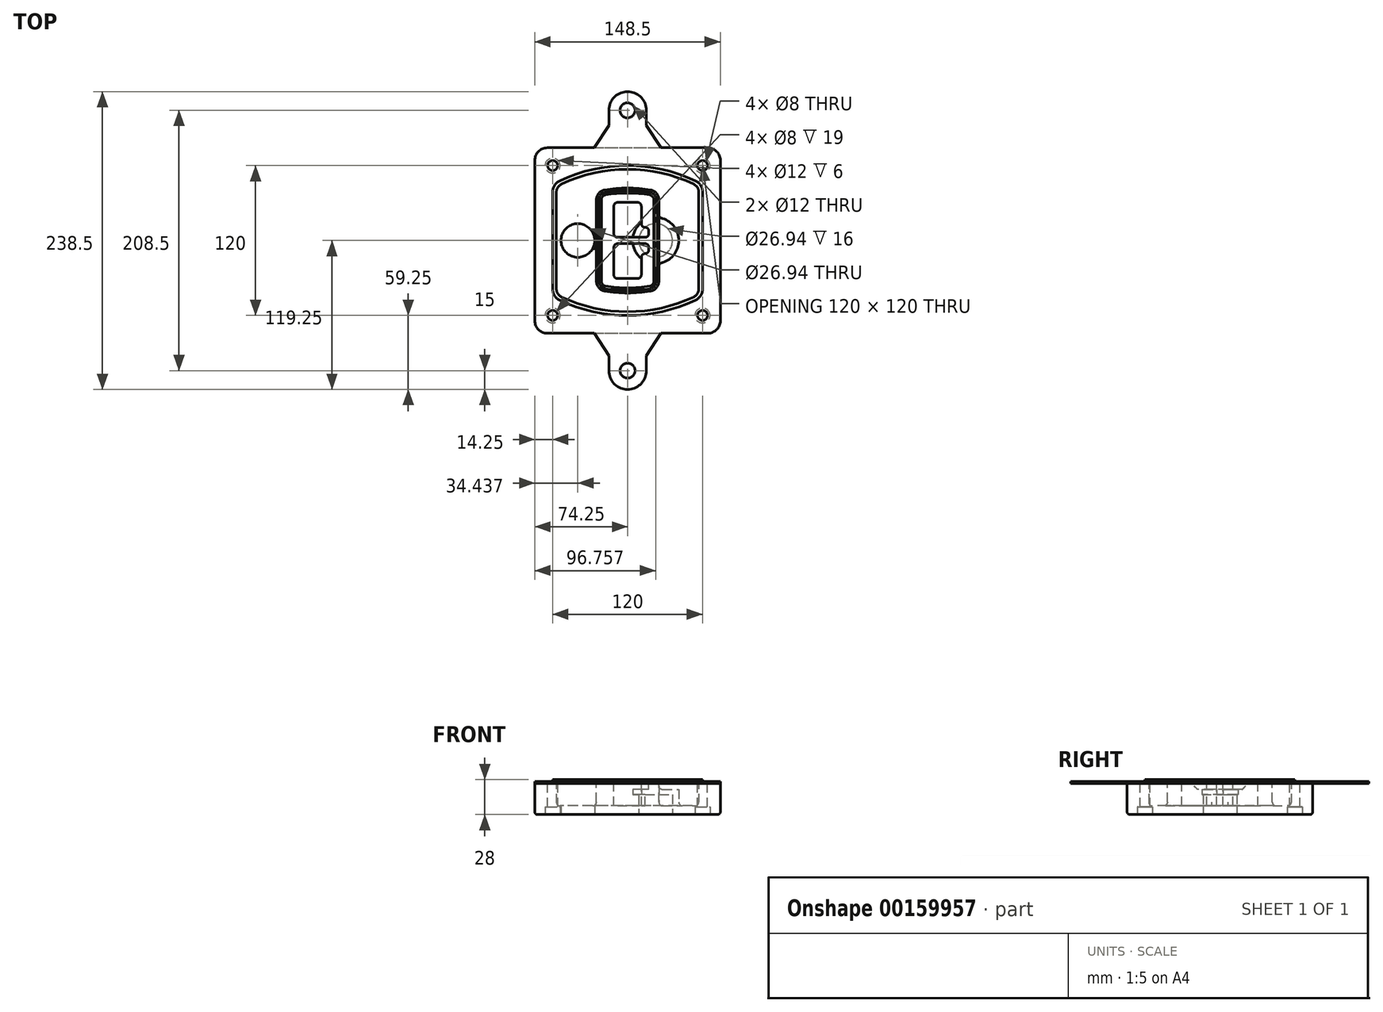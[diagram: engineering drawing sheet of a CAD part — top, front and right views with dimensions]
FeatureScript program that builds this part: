
annotation { "Feature Type Name" : "Feature", "Feature Type Description" : "" }
export const myFeature = defineFeature(function(context is Context, id is Id, definition is map)
    precondition{}
    {
        {
            var Q0;
            Q0=qCreatedBy(makeId("Top.planeOp"),FACE);
            var sketch = newSketch(context, id + "F0", { "sketchPlane" : qUnion([Q0])});
            skPoint(sketch, "E0.rect.middle", {"position": v(0, 0) * mm});
            skLineSegment(sketch, "E1.bottom", {"start": v(-64.25, -74.25) * mm, "end": v(64.25, -74.25) * mm});
            skLineSegment(sketch, "E1.top", {"start": v(-64.25, 74.25) * mm, "end": v(64.25, 74.25) * mm});
            skLineSegment(sketch, "E1.left", {"start": v(-74.25, -64.25) * mm, "end": v(-74.25, 64.25) * mm});
            skLineSegment(sketch, "E1.right", {"start": v(74.25, -64.25) * mm, "end": v(74.25, 64.25) * mm});
            skLineSegment(sketch, "E2", {"start": v(-74.25, 74.25) * mm, "end": v(74.25, -74.25) * mm, "construction": true});
            skLineSegment(sketch, "E3", {"start": v(74.25, 74.25) * mm, "end": v(-74.25, -74.25) * mm, "construction": true});
            skCircle(sketch, "E4", {"center": v(-60, 60) * mm, "radius": 4 * mm});
            skCircle(sketch, "E5", {"center": v(60, 60) * mm, "radius": 4 * mm});
            skCircle(sketch, "E6", {"center": v(60, -60) * mm, "radius": 4 * mm});
            skCircle(sketch, "E7", {"center": v(-60, -60) * mm, "radius": 4 * mm});
            skLineSegment(sketch, "E8", {"start": v(-60, 60) * mm, "end": v(60, 60) * mm, "construction": true});
            skLineSegment(sketch, "E9", {"start": v(60, 60) * mm, "end": v(60, -60) * mm, "construction": true});
            skLineSegment(sketch, "E10", {"start": v(60, -60) * mm, "end": v(-60, -60) * mm, "construction": true});
            skLineSegment(sketch, "E11", {"start": v(-60, -60) * mm, "end": v(-60, 60) * mm, "construction": true});
            skLineSegment(sketch, "E12", {"start": v(-60, 38.83) * mm, "end": v(-60, -38.83) * mm});
            skLineSegment(sketch, "E13", {"start": v(60, 38.83) * mm, "end": v(60, -38.83) * mm});
            skArc(sketch, "E14", {"start": v(54.26, 47.88) * mm, "mid": v(0, 60) * mm, "end": v(-54.26, 47.88) * mm});
            skArc(sketch, "E15", {"start": v(-54.26, -47.88) * mm, "mid": v(0, -60) * mm, "end": v(54.26, -47.88) * mm});
            skLineSegment(sketch, "E16", {"start": v(-60, 0) * mm, "end": v(60, 0) * mm, "construction": true});
            skPoint(sketch, "E17.visualSharp", {"position": v(-60, -45) * mm});
            skArc(sketch, "E17.filletArc", {"start": v(-60, -38.83) * mm, "mid": v(-58.44, -44.2) * mm, "end": v(-54.26, -47.88) * mm});
            skPoint(sketch, "E18.visualSharp", {"position": v(-60, 45) * mm});
            skArc(sketch, "E18.filletArc", {"start": v(-54.26, 47.88) * mm, "mid": v(-58.44, 44.2) * mm, "end": v(-60, 38.83) * mm});
            skPoint(sketch, "E19.visualSharp", {"position": v(60, 45) * mm});
            skArc(sketch, "E19.filletArc", {"start": v(60, 38.83) * mm, "mid": v(58.44, 44.2) * mm, "end": v(54.26, 47.88) * mm});
            skPoint(sketch, "E20.visualSharp", {"position": v(60, -45) * mm});
            skArc(sketch, "E20.filletArc", {"start": v(54.26, -47.88) * mm, "mid": v(58.44, -44.2) * mm, "end": v(60, -38.83) * mm});
            skPoint(sketch, "E21.visualSharp", {"position": v(-74.25, 74.25) * mm});
            skArc(sketch, "E21.filletArc", {"start": v(-64.25, 74.25) * mm, "mid": v(-71.32, 71.32) * mm, "end": v(-74.25, 64.25) * mm});
            skPoint(sketch, "E22.visualSharp", {"position": v(74.25, 74.25) * mm});
            skArc(sketch, "E22.filletArc", {"start": v(74.25, 64.25) * mm, "mid": v(71.32, 71.32) * mm, "end": v(64.25, 74.25) * mm});
            skPoint(sketch, "E23.visualSharp", {"position": v(74.25, -74.25) * mm});
            skArc(sketch, "E23.filletArc", {"start": v(64.25, -74.25) * mm, "mid": v(71.32, -71.32) * mm, "end": v(74.25, -64.25) * mm});
            skPoint(sketch, "E24.visualSharp", {"position": v(-74.25, -74.25) * mm});
            skArc(sketch, "E24.filletArc", {"start": v(-74.25, -64.25) * mm, "mid": v(-71.32, -71.32) * mm, "end": v(-64.25, -74.25) * mm});
            skArc(sketch, "E25.0", {"start": v(57, 38.83) * mm, "mid": v(55.9, 42.58) * mm, "end": v(52.98, 45.17) * mm});
            skLineSegment(sketch, "E25.1", {"start": v(57, 38.83) * mm, "end": v(57, -38.83) * mm});
            skArc(sketch, "E25.2", {"start": v(52.98, -45.17) * mm, "mid": v(55.9, -42.58) * mm, "end": v(57, -38.83) * mm});
            skArc(sketch, "E25.3", {"start": v(-52.98, -45.17) * mm, "mid": v(0, -57) * mm, "end": v(52.98, -45.17) * mm});
            skArc(sketch, "E25.4", {"start": v(-57, -38.83) * mm, "mid": v(-55.9, -42.58) * mm, "end": v(-52.98, -45.17) * mm});
            skArc(sketch, "E25.5", {"start": v(52.98, 45.17) * mm, "mid": v(0, 57) * mm, "end": v(-52.98, 45.17) * mm});
            skLineSegment(sketch, "E25.6", {"start": v(-57, 38.83) * mm, "end": v(-57, -38.83) * mm});
            skArc(sketch, "E25.7", {"start": v(-52.98, 45.17) * mm, "mid": v(-55.9, 42.58) * mm, "end": v(-57, 38.83) * mm});
            skArc(sketch, "E26.0", {"start": v(-55.96, 51.5) * mm, "mid": v(-61.82, 46.33) * mm, "end": v(-64, 38.83) * mm});
            skArc(sketch, "E26.1", {"start": v(55.96, 51.5) * mm, "mid": v(0, 64) * mm, "end": v(-55.96, 51.5) * mm});
            skArc(sketch, "E26.2", {"start": v(64, 38.83) * mm, "mid": v(61.82, 46.33) * mm, "end": v(55.96, 51.5) * mm});
            skLineSegment(sketch, "E26.3", {"start": v(64, 38.83) * mm, "end": v(64, -38.83) * mm});
            skArc(sketch, "E26.4", {"start": v(55.96, -51.5) * mm, "mid": v(61.82, -46.33) * mm, "end": v(64, -38.83) * mm});
            skLineSegment(sketch, "E26.5", {"start": v(-64, 38.83) * mm, "end": v(-64, -38.83) * mm});
            skArc(sketch, "E26.6", {"start": v(-55.96, -51.5) * mm, "mid": v(0, -64) * mm, "end": v(55.96, -51.5) * mm});
            skArc(sketch, "E26.7", {"start": v(-64, -38.83) * mm, "mid": v(-61.82, -46.33) * mm, "end": v(-55.96, -51.5) * mm});
            skSolve(sketch);
        }
        {
            var Q0;
            Q0=makeQuery(id+"F0.imprint","IMPRINT",FACE,{"disambiguationData":[TD([[makeQuery(id+"F0.imprint","IMPRINT",EDGE,{"derivedFrom":sQuery(id+"F0.wireOp",EDGE,"E1.bottom")}),1.0]])]});
            var Q1;
            Q1=makeQuery(id+"F0.imprint","IMPRINT",FACE,{"disambiguationData":[TD([[makeQuery(id+"F0.imprint","IMPRINT",EDGE,{"derivedFrom":sQuery(id+"F0.wireOp",EDGE,"E12")}),1.0]])]});
            var Q2;
            Q2=makeQuery(id+"F0.imprint","IMPRINT",FACE,{"disambiguationData":[TD([[makeQuery(id+"F0.imprint","IMPRINT",EDGE,{"derivedFrom":sQuery(id+"F0.wireOp",EDGE,"E25.0")}),1.0]])]});
            var Q3;
            Q3=makeQuery(id+"F0.imprint","IMPRINT",FACE,{"disambiguationData":[TD([[makeQuery(id+"F0.imprint","IMPRINT",EDGE,{"derivedFrom":sQuery(id+"F0.wireOp",EDGE,"E12")}),-1.0]])]});
            extrude(context, id + "F1", {"entities" : qUnion([Q0, Q1, Q2, Q3]), "oppositeDirection" : true, "depth" : 25 * mm});
        }
        {
            var Q0;
            Q0=makeQuery(id+"F0.imprint","IMPRINT",FACE,{"disambiguationData":[TD([[makeQuery(id+"F0.imprint","IMPRINT",EDGE,{"derivedFrom":sQuery(id+"F0.wireOp",EDGE,"E12")}),1.0]])]});
            extrude(context, id + "F2", {"entities" : qUnion([Q0]), "operationType" : NewBodyOperationType.ADD, "depth" : 3 * mm});
        }
        {
            var Q0;
            Q0=makeQuery(id+"F0.imprint","IMPRINT",FACE,{"disambiguationData":[TD([[makeQuery(id+"F0.imprint","IMPRINT",EDGE,{"derivedFrom":sQuery(id+"F0.wireOp",EDGE,"E25.0")}),1.0]])]});
            extrude(context, id + "F3", {"entities" : qUnion([Q0]), "operationType" : NewBodyOperationType.REMOVE, "oppositeDirection" : true, "depth" : 18 * mm});
        }
        {
            var Q0;
            Q0=makeQuery(id+"F2.opExtrude","CAP_FACE",FACE,{"disambiguationData":[OSD([sQuery(id+"F0.wireOp",EDGE,"E12"),sQuery(id+"F0.wireOp",EDGE,"E13"),sQuery(id+"F0.wireOp",EDGE,"E14"),sQuery(id+"F0.wireOp",EDGE,"E15"),sQuery(id+"F0.wireOp",EDGE,"E17.filletArc"),sQuery(id+"F0.wireOp",EDGE,"E18.filletArc"),sQuery(id+"F0.wireOp",EDGE,"E19.filletArc"),sQuery(id+"F0.wireOp",EDGE,"E20.filletArc"),sQuery(id+"F0.wireOp",EDGE,"E25.0"),sQuery(id+"F0.wireOp",EDGE,"E25.1"),sQuery(id+"F0.wireOp",EDGE,"E25.2"),sQuery(id+"F0.wireOp",EDGE,"E25.3"),sQuery(id+"F0.wireOp",EDGE,"E25.4"),sQuery(id+"F0.wireOp",EDGE,"E25.5"),sQuery(id+"F0.wireOp",EDGE,"E25.6"),sQuery(id+"F0.wireOp",EDGE,"E25.7")])],"isStart":false});
            var sketch = newSketch(context, id + "F4", { "sketchPlane" : qUnion([Q0])});
            skArc(sketch, "E27.0", {"start": v(-18.34, -40.45) * mm, "mid": v(0, -42) * mm, "end": v(18.34, -40.45) * mm});
            skArc(sketch, "E28.0", {"start": v(18.34, 40.45) * mm, "mid": v(0, 42) * mm, "end": v(-18.34, 40.45) * mm});
            skLineSegment(sketch, "E29", {"start": v(-25, 32.57) * mm, "end": v(-25, -32.57) * mm});
            skLineSegment(sketch, "E30", {"start": v(25, 32.57) * mm, "end": v(25, -32.57) * mm});
            skLineSegment(sketch, "E31", {"start": v(-25, 39.1) * mm, "end": v(25, 39.1) * mm, "construction": true});
            skLineSegment(sketch, "E32", {"start": v(-25, -39.1) * mm, "end": v(25, -39.1) * mm, "construction": true});
            skPoint(sketch, "E33.visualSharp", {"position": v(-25, 39.1) * mm});
            skArc(sketch, "E33.filletArc", {"start": v(-18.34, 40.45) * mm, "mid": v(-23.11, 37.73) * mm, "end": v(-25, 32.57) * mm});
            skPoint(sketch, "E34.visualSharp", {"position": v(25, 39.1) * mm});
            skArc(sketch, "E34.filletArc", {"start": v(25, 32.57) * mm, "mid": v(23.11, 37.73) * mm, "end": v(18.34, 40.45) * mm});
            skPoint(sketch, "E35.visualSharp", {"position": v(25, -39.1) * mm});
            skArc(sketch, "E35.filletArc", {"start": v(18.34, -40.45) * mm, "mid": v(23.11, -37.73) * mm, "end": v(25, -32.57) * mm});
            skPoint(sketch, "E36.visualSharp", {"position": v(-25, -39.1) * mm});
            skArc(sketch, "E36.filletArc", {"start": v(-25, -32.57) * mm, "mid": v(-23.11, -37.73) * mm, "end": v(-18.34, -40.45) * mm});
            skArc(sketch, "E37.0", {"start": v(52.98, 45.17) * mm, "mid": v(0, 57) * mm, "end": v(-52.98, 45.17) * mm});
            skArc(sketch, "E37.1", {"start": v(-52.98, 45.17) * mm, "mid": v(-55.9, 42.58) * mm, "end": v(-57, 38.83) * mm});
            skLineSegment(sketch, "E37.2", {"start": v(-57, 38.83) * mm, "end": v(-57, -38.83) * mm});
            skArc(sketch, "E37.3", {"start": v(-57, -38.83) * mm, "mid": v(-55.9, -42.58) * mm, "end": v(-52.98, -45.17) * mm});
            skArc(sketch, "E37.4", {"start": v(-52.98, -45.17) * mm, "mid": v(0, -57) * mm, "end": v(52.98, -45.17) * mm});
            skArc(sketch, "E37.5", {"start": v(52.98, -45.17) * mm, "mid": v(55.9, -42.58) * mm, "end": v(57, -38.83) * mm});
            skLineSegment(sketch, "E37.6", {"start": v(57, 38.83) * mm, "end": v(57, -38.83) * mm});
            skArc(sketch, "E37.7", {"start": v(57, 38.83) * mm, "mid": v(55.9, 42.58) * mm, "end": v(52.98, 45.17) * mm});
            skLineSegment(sketch, "E38.0", {"start": v(23, 32.57) * mm, "end": v(23, -32.57) * mm});
            skArc(sketch, "E38.1", {"start": v(18, -38.48) * mm, "mid": v(21.58, -36.44) * mm, "end": v(23, -32.57) * mm});
            skArc(sketch, "E38.2", {"start": v(-18, -38.48) * mm, "mid": v(0, -40) * mm, "end": v(18, -38.48) * mm});
            skArc(sketch, "E38.3", {"start": v(-23, -32.57) * mm, "mid": v(-21.58, -36.44) * mm, "end": v(-18, -38.48) * mm});
            skLineSegment(sketch, "E38.4", {"start": v(-23, 32.57) * mm, "end": v(-23, -32.57) * mm});
            skArc(sketch, "E38.5", {"start": v(23, 32.57) * mm, "mid": v(21.58, 36.44) * mm, "end": v(18, 38.48) * mm});
            skArc(sketch, "E38.6", {"start": v(-18, 38.48) * mm, "mid": v(-21.58, 36.44) * mm, "end": v(-23, 32.57) * mm});
            skArc(sketch, "E38.7", {"start": v(18, 38.48) * mm, "mid": v(0, 40) * mm, "end": v(-18, 38.48) * mm});
            skArc(sketch, "E39.0", {"start": v(21, 32.57) * mm, "mid": v(20.06, 35.15) * mm, "end": v(17.67, 36.5) * mm});
            skLineSegment(sketch, "E39.1", {"start": v(21, 32.57) * mm, "end": v(21, -32.57) * mm});
            skArc(sketch, "E39.2", {"start": v(17.67, -36.5) * mm, "mid": v(20.06, -35.15) * mm, "end": v(21, -32.57) * mm});
            skArc(sketch, "E39.3", {"start": v(-17.67, -36.5) * mm, "mid": v(0, -38) * mm, "end": v(17.67, -36.5) * mm});
            skArc(sketch, "E39.4", {"start": v(-21, -32.57) * mm, "mid": v(-20.06, -35.15) * mm, "end": v(-17.67, -36.5) * mm});
            skArc(sketch, "E39.5", {"start": v(17.67, 36.5) * mm, "mid": v(0, 38) * mm, "end": v(-17.67, 36.5) * mm});
            skLineSegment(sketch, "E39.6", {"start": v(-21, 32.57) * mm, "end": v(-21, -32.57) * mm});
            skArc(sketch, "E39.7", {"start": v(-17.67, 36.5) * mm, "mid": v(-20.06, 35.15) * mm, "end": v(-21, 32.57) * mm});
            skLineSegment(sketch, "E40", {"start": v(-25, 0) * mm, "end": v(25, 0) * mm, "construction": true});
            skLineSegment(sketch, "E41", {"start": v(-11, 5.5) * mm, "end": v(-11, 27.5) * mm});
            skLineSegment(sketch, "E42", {"start": v(-8, 30.5) * mm, "end": v(8, 30.5) * mm});
            skLineSegment(sketch, "E43", {"start": v(11, 27.5) * mm, "end": v(11, 13.5) * mm});
            skLineSegment(sketch, "E44", {"start": v(14, 10.5) * mm, "end": v(14, 10.5) * mm});
            skLineSegment(sketch, "E45", {"start": v(17, 7.5) * mm, "end": v(17, 5.5) * mm});
            skLineSegment(sketch, "E46", {"start": v(14, 2.5) * mm, "end": v(-8, 2.5) * mm});
            skPoint(sketch, "E47.visualSharp", {"position": v(-11, 30.5) * mm});
            skArc(sketch, "E47.filletArc", {"start": v(-8, 30.5) * mm, "mid": v(-10.12, 29.62) * mm, "end": v(-11, 27.5) * mm});
            skPoint(sketch, "E48.visualSharp", {"position": v(11, 30.5) * mm});
            skArc(sketch, "E48.filletArc", {"start": v(11, 27.5) * mm, "mid": v(10.12, 29.62) * mm, "end": v(8, 30.5) * mm});
            skPoint(sketch, "E49.visualSharp", {"position": v(11, 10.5) * mm});
            skArc(sketch, "E49.filletArc", {"start": v(11, 13.5) * mm, "mid": v(11.88, 11.38) * mm, "end": v(14, 10.5) * mm});
            skPoint(sketch, "E50.visualSharp", {"position": v(17, 10.5) * mm});
            skArc(sketch, "E50.filletArc", {"start": v(17, 7.5) * mm, "mid": v(16.12, 9.62) * mm, "end": v(14, 10.5) * mm});
            skPoint(sketch, "E51.visualSharp", {"position": v(17, 2.5) * mm});
            skArc(sketch, "E51.filletArc", {"start": v(14, 2.5) * mm, "mid": v(16.12, 3.38) * mm, "end": v(17, 5.5) * mm});
            skPoint(sketch, "E52.visualSharp", {"position": v(-11, 2.5) * mm});
            skArc(sketch, "E52.filletArc", {"start": v(-11, 5.5) * mm, "mid": v(-10.12, 3.38) * mm, "end": v(-8, 2.5) * mm});
            skLineSegment(sketch, "E53.0.MirrorCS", {"start": v(14, -2.5) * mm, "end": v(-8, -2.5) * mm});
            skArc(sketch, "E54.0.MirrorCS", {"start": v(-11, -5.5) * mm, "mid": v(-10.12, -3.38) * mm, "end": v(-8, -2.5) * mm});
            skLineSegment(sketch, "E55.0.MirrorCS", {"start": v(-11, -5.5) * mm, "end": v(-11, -27.5) * mm});
            skArc(sketch, "E56.0.MirrorCS", {"start": v(-8, -30.5) * mm, "mid": v(-10.12, -29.62) * mm, "end": v(-11, -27.5) * mm});
            skLineSegment(sketch, "E57.0.MirrorCS", {"start": v(-8, -30.5) * mm, "end": v(8, -30.5) * mm});
            skArc(sketch, "E58.0.MirrorCS", {"start": v(11, -27.5) * mm, "mid": v(10.12, -29.62) * mm, "end": v(8, -30.5) * mm});
            skLineSegment(sketch, "E59.0.MirrorCS", {"start": v(11, -27.5) * mm, "end": v(11, -13.5) * mm});
            skArc(sketch, "E60.0.MirrorCS", {"start": v(11, -13.5) * mm, "mid": v(11.88, -11.38) * mm, "end": v(14, -10.5) * mm});
            skArc(sketch, "E61.0.MirrorCS", {"start": v(17, -7.5) * mm, "mid": v(16.12, -9.62) * mm, "end": v(14, -10.5) * mm});
            skLineSegment(sketch, "E62.0.MirrorCS", {"start": v(17, -7.5) * mm, "end": v(17, -5.5) * mm});
            skArc(sketch, "E63.0.MirrorCS", {"start": v(14, -2.5) * mm, "mid": v(16.12, -3.38) * mm, "end": v(17, -5.5) * mm});
            skSolve(sketch);
        }
        {
            var Q0;
            Q0=makeQuery(id+"F4.imprint","IMPRINT",FACE,{"disambiguationData":[TD([[makeQuery(id+"F4.imprint","IMPRINT",EDGE,{"derivedFrom":sQuery(id+"F4.wireOp",EDGE,"E27.0")}),1.0]])]});
            var Q1;
            Q1=makeQuery(id+"F4.imprint","IMPRINT",FACE,{"disambiguationData":[TD([[makeQuery(id+"F4.imprint","IMPRINT",EDGE,{"derivedFrom":sQuery(id+"F4.wireOp",EDGE,"E38.0")}),-1.0]])]});
            var Q2;
            Q2=makeQuery(id+"F4.imprint","IMPRINT",FACE,{"disambiguationData":[TD([[makeQuery(id+"F4.imprint","IMPRINT",EDGE,{"derivedFrom":sQuery(id+"F4.wireOp",EDGE,"E39.0")}),1.0]])]});
            extrude(context, id + "F5", {"entities" : qUnion([Q0, Q1, Q2]), "operationType" : NewBodyOperationType.ADD, "endBound" : BoundingType.UP_TO_NEXT, "oppositeDirection" : true, "depth" : 25 * mm});
        }
        {
            var Q0;
            Q0=makeQuery(id+"F4.imprint","IMPRINT",FACE,{"disambiguationData":[TD([[makeQuery(id+"F4.imprint","IMPRINT",EDGE,{"derivedFrom":sQuery(id+"F4.wireOp",EDGE,"E38.0")}),-1.0]])]});
            extrude(context, id + "F6", {"entities" : qUnion([Q0]), "operationType" : NewBodyOperationType.REMOVE, "oppositeDirection" : true, "depth" : 2 * mm});
        }
        {
            var Q0;
            Q0=makeQuery(id+"F1.opExtrude","CAP_FACE",FACE,{"disambiguationData":[OSD([sQuery(id+"F0.wireOp",EDGE,"E1.bottom"),sQuery(id+"F0.wireOp",EDGE,"E1.top"),sQuery(id+"F0.wireOp",EDGE,"E1.left"),sQuery(id+"F0.wireOp",EDGE,"E1.right"),sQuery(id+"F0.wireOp",EDGE,"E4"),sQuery(id+"F0.wireOp",EDGE,"E5"),sQuery(id+"F0.wireOp",EDGE,"E6"),sQuery(id+"F0.wireOp",EDGE,"E7"),sQuery(id+"F0.wireOp",EDGE,"E21.filletArc"),sQuery(id+"F0.wireOp",EDGE,"E22.filletArc"),sQuery(id+"F0.wireOp",EDGE,"E23.filletArc"),sQuery(id+"F0.wireOp",EDGE,"E24.filletArc")])],"isStart":false});
            var sketch = newSketch(context, id + "F7", { "sketchPlane" : qUnion([Q0])});
            skCircle(sketch, "E64", {"center": v(22.5, 0) * mm, "radius": 13.47 * mm});
            skCircle(sketch, "E65", {"center": v(-39.81, 0) * mm, "radius": 13.47 * mm});
            skLineSegment(sketch, "E66", {"start": v(74.25, 0) * mm, "end": v(-74.25, 0) * mm});
            skCircle(sketch, "E67", {"center": v(22.5, 0) * mm, "radius": 18.47 * mm});
            skCircle(sketch, "E68", {"center": v(60, -60) * mm, "radius": 6 * mm});
            skCircle(sketch, "E69", {"center": v(-60, -60) * mm, "radius": 6 * mm});
            skCircle(sketch, "E70", {"center": v(-60, 60) * mm, "radius": 6 * mm});
            skCircle(sketch, "E71", {"center": v(60, 60) * mm, "radius": 6 * mm});
            skSolve(sketch);
        }
        {
            var Q0;
            {var subQ1=sQuery(id+"F7.wireOp",EDGE,"E66");var subQ4=sQuery(id+"F7.wireOp",EDGE,"E64");var subQ6=makeQuery(id+"F7.imprint","INTERSECT",VERTEX,{"disambiguationData":[OD(0.0)],"derivedFrom":[subQ4,subQ1]});Q0=makeQuery(id+"F7.imprint","IMPRINT",FACE,{"disambiguationData":[TD([[makeQuery(id+"F7.imprint","IMPRINT",EDGE,{"disambiguationData":[TD([[subQ6,-1.0]])],"derivedFrom":subQ4}),-1.0]])]});}
            var Q1;
            {var subQ0=sQuery(id+"F7.wireOp",EDGE,"E66");var subQ1=sQuery(id+"F7.wireOp",EDGE,"E64");var subQ3=makeQuery(id+"F7.imprint","INTERSECT",VERTEX,{"disambiguationData":[OD(0.0)],"derivedFrom":[subQ1,subQ0]});Q1=makeQuery(id+"F7.imprint","IMPRINT",FACE,{"disambiguationData":[TD([[makeQuery(id+"F7.imprint","IMPRINT",EDGE,{"disambiguationData":[TD([[subQ3,-1.0]])],"derivedFrom":subQ1}),1.0]])]});}
            var Q2;
            {var subQ0=sQuery(id+"F7.wireOp",EDGE,"E66");var subQ1=sQuery(id+"F7.wireOp",EDGE,"E64");var subQ3=makeQuery(id+"F7.imprint","INTERSECT",VERTEX,{"disambiguationData":[OD(0.0)],"derivedFrom":[subQ1,subQ0]});Q2=makeQuery(id+"F7.imprint","IMPRINT",FACE,{"disambiguationData":[TD([[makeQuery(id+"F7.imprint","IMPRINT",EDGE,{"disambiguationData":[TD([[subQ3,1.0]])],"derivedFrom":subQ1}),1.0]])]});}
            var Q3;
            {var subQ1=sQuery(id+"F7.wireOp",EDGE,"E66");var subQ4=sQuery(id+"F7.wireOp",EDGE,"E64");var subQ6=makeQuery(id+"F7.imprint","INTERSECT",VERTEX,{"disambiguationData":[OD(0.0)],"derivedFrom":[subQ4,subQ1]});Q3=makeQuery(id+"F7.imprint","IMPRINT",FACE,{"disambiguationData":[TD([[makeQuery(id+"F7.imprint","IMPRINT",EDGE,{"disambiguationData":[TD([[subQ6,1.0]])],"derivedFrom":subQ4}),-1.0]])]});}
            extrude(context, id + "F8", {"entities" : qUnion([Q0, Q1, Q2, Q3]), "operationType" : NewBodyOperationType.ADD, "oppositeDirection" : true, "depth" : 20 * mm});
        }
        {
            var Q0;
            {var subQ0=sQuery(id+"F7.wireOp",EDGE,"E66");var subQ1=sQuery(id+"F7.wireOp",EDGE,"E64");var subQ3=makeQuery(id+"F7.imprint","INTERSECT",VERTEX,{"disambiguationData":[OD(0.0)],"derivedFrom":[subQ1,subQ0]});Q0=makeQuery(id+"F7.imprint","IMPRINT",FACE,{"disambiguationData":[TD([[makeQuery(id+"F7.imprint","IMPRINT",EDGE,{"disambiguationData":[TD([[subQ3,-1.0]])],"derivedFrom":subQ1}),1.0]])]});}
            var Q1;
            {var subQ0=sQuery(id+"F7.wireOp",EDGE,"E66");var subQ1=sQuery(id+"F7.wireOp",EDGE,"E64");var subQ3=makeQuery(id+"F7.imprint","INTERSECT",VERTEX,{"disambiguationData":[OD(0.0)],"derivedFrom":[subQ1,subQ0]});Q1=makeQuery(id+"F7.imprint","IMPRINT",FACE,{"disambiguationData":[TD([[makeQuery(id+"F7.imprint","IMPRINT",EDGE,{"disambiguationData":[TD([[subQ3,1.0]])],"derivedFrom":subQ1}),1.0]])]});}
            extrude(context, id + "F9", {"entities" : qUnion([Q0, Q1]), "operationType" : NewBodyOperationType.REMOVE, "oppositeDirection" : true, "depth" : 16 * mm});
        }
        {
            var Q0;
            {var subQ0=sQuery(id+"F7.wireOp",EDGE,"E66");var subQ1=sQuery(id+"F7.wireOp",EDGE,"E65");var subQ3=makeQuery(id+"F7.imprint","INTERSECT",VERTEX,{"disambiguationData":[OD(0.0)],"derivedFrom":[subQ1,subQ0]});Q0=makeQuery(id+"F7.imprint","IMPRINT",FACE,{"disambiguationData":[TD([[makeQuery(id+"F7.imprint","IMPRINT",EDGE,{"disambiguationData":[TD([[subQ3,-1.0]])],"derivedFrom":subQ1}),1.0]])]});}
            var Q1;
            {var subQ0=sQuery(id+"F7.wireOp",EDGE,"E66");var subQ1=sQuery(id+"F7.wireOp",EDGE,"E65");var subQ3=makeQuery(id+"F7.imprint","INTERSECT",VERTEX,{"disambiguationData":[OD(0.0)],"derivedFrom":[subQ1,subQ0]});Q1=makeQuery(id+"F7.imprint","IMPRINT",FACE,{"disambiguationData":[TD([[makeQuery(id+"F7.imprint","IMPRINT",EDGE,{"disambiguationData":[TD([[subQ3,1.0]])],"derivedFrom":subQ1}),1.0]])]});}
            extrude(context, id + "F10", {"entities" : qUnion([Q0, Q1]), "operationType" : NewBodyOperationType.REMOVE, "oppositeDirection" : true, "depth" : 25 * mm});
        }
        {
            var Q0;
            Q0=makeQuery(id+"F7.imprint","IMPRINT",FACE,{"disambiguationData":[TD([[makeQuery(id+"F7.imprint","IMPRINT",EDGE,{"derivedFrom":sQuery(id+"F7.wireOp",EDGE,"E68")}),1.0]])]});
            var Q1;
            Q1=makeQuery(id+"F7.imprint","IMPRINT",FACE,{"disambiguationData":[TD([[makeQuery(id+"F7.imprint","IMPRINT",EDGE,{"derivedFrom":makeQuery(id+"F1.opExtrude","CAP_EDGE",EDGE,{"disambiguationData":[OSD([sQuery(id+"F0.wireOp",EDGE,"E5")])],"isStart":false})}),-1.0]])]});
            var Q2;
            Q2=makeQuery(id+"F7.imprint","IMPRINT",FACE,{"disambiguationData":[TD([[makeQuery(id+"F7.imprint","IMPRINT",EDGE,{"derivedFrom":sQuery(id+"F7.wireOp",EDGE,"E69")}),1.0]])]});
            var Q3;
            Q3=makeQuery(id+"F7.imprint","IMPRINT",FACE,{"disambiguationData":[TD([[makeQuery(id+"F7.imprint","IMPRINT",EDGE,{"derivedFrom":makeQuery(id+"F1.opExtrude","CAP_EDGE",EDGE,{"disambiguationData":[OSD([sQuery(id+"F0.wireOp",EDGE,"E4")])],"isStart":false})}),-1.0]])]});
            var Q4;
            Q4=makeQuery(id+"F7.imprint","IMPRINT",FACE,{"disambiguationData":[TD([[makeQuery(id+"F7.imprint","IMPRINT",EDGE,{"derivedFrom":sQuery(id+"F7.wireOp",EDGE,"E70")}),1.0]])]});
            var Q5;
            Q5=makeQuery(id+"F7.imprint","IMPRINT",FACE,{"disambiguationData":[TD([[makeQuery(id+"F7.imprint","IMPRINT",EDGE,{"derivedFrom":makeQuery(id+"F1.opExtrude","CAP_EDGE",EDGE,{"disambiguationData":[OSD([sQuery(id+"F0.wireOp",EDGE,"E7")])],"isStart":false})}),-1.0]])]});
            var Q6;
            Q6=makeQuery(id+"F7.imprint","IMPRINT",FACE,{"disambiguationData":[TD([[makeQuery(id+"F7.imprint","IMPRINT",EDGE,{"derivedFrom":sQuery(id+"F7.wireOp",EDGE,"E71")}),1.0]])]});
            var Q7;
            Q7=makeQuery(id+"F7.imprint","IMPRINT",FACE,{"disambiguationData":[TD([[makeQuery(id+"F7.imprint","IMPRINT",EDGE,{"derivedFrom":makeQuery(id+"F1.opExtrude","CAP_EDGE",EDGE,{"disambiguationData":[OSD([sQuery(id+"F0.wireOp",EDGE,"E6")])],"isStart":false})}),-1.0]])]});
            extrude(context, id + "F11", {"entities" : qUnion([Q0, Q1, Q2, Q3, Q4, Q5, Q6, Q7]), "operationType" : NewBodyOperationType.REMOVE, "oppositeDirection" : true, "depth" : 6 * mm});
        }
        {
            var Q0;
            Q0=makeQuery(id+"F9.boolean.opBoolean","COPY",FACE,{"derivedFrom":makeQuery(id+"F9.opExtrude","CAP_FACE",FACE,{"disambiguationData":[OSD([sQuery(id+"F7.wireOp",EDGE,"E64")])],"isStart":false})});
            var sketch = newSketch(context, id + "F12", { "sketchPlane" : qUnion([Q0])});
            skArc(sketch, "E72.0", {"start": v(11, 14.45) * mm, "mid": v(6.45, 9.13) * mm, "end": v(4.2, 2.5) * mm});
            skArc(sketch, "E72.1", {"start": v(4.2, -2.5) * mm, "mid": v(6.45, -9.13) * mm, "end": v(11, -14.45) * mm});
            skLineSegment(sketch, "E73", {"start": v(4.2, -2.5) * mm, "end": v(14, -2.5) * mm});
            skLineSegment(sketch, "E74.0", {"start": v(14, 2.5) * mm, "end": v(4.2, 2.5) * mm});
            skArc(sketch, "E74.1", {"start": v(14, 2.5) * mm, "mid": v(16.12, 3.38) * mm, "end": v(17, 5.5) * mm});
            skLineSegment(sketch, "E74.2", {"start": v(17, 7.5) * mm, "end": v(17, 5.5) * mm});
            skArc(sketch, "E74.3", {"start": v(17, 7.5) * mm, "mid": v(16.12, 9.62) * mm, "end": v(14, 10.5) * mm});
            skArc(sketch, "E74.4", {"start": v(11, 13.5) * mm, "mid": v(11.88, 11.38) * mm, "end": v(14, 10.5) * mm});
            skLineSegment(sketch, "E74.5", {"start": v(11, 14.45) * mm, "end": v(11, 13.5) * mm});
            skLineSegment(sketch, "E74.7", {"start": v(14, -2.5) * mm, "end": v(4.2, -2.5) * mm});
            skArc(sketch, "E74.8", {"start": v(14, -2.5) * mm, "mid": v(16.12, -3.38) * mm, "end": v(17, -5.5) * mm});
            skLineSegment(sketch, "E74.9", {"start": v(17, -7.5) * mm, "end": v(17, -5.5) * mm});
            skArc(sketch, "E74.10", {"start": v(17, -7.5) * mm, "mid": v(16.12, -9.62) * mm, "end": v(14, -10.5) * mm});
            skArc(sketch, "E74.11", {"start": v(11, -13.5) * mm, "mid": v(11.88, -11.38) * mm, "end": v(14, -10.5) * mm});
            skLineSegment(sketch, "E74.12", {"start": v(11, -14.45) * mm, "end": v(11, -13.5) * mm});
            skPoint(sketch, "E75.orphan", {"position": v(11, -27.5) * mm});
            skPoint(sketch, "E76.orphan", {"position": v(-8, -2.5) * mm});
            skPoint(sketch, "E77.orphan", {"position": v(-8, 2.5) * mm});
            skPoint(sketch, "E78.orphan", {"position": v(11, 27.5) * mm});
            skSolve(sketch);
        }
        {
            var Q0;
            {var subQ7=sQuery(id+"F12.wireOp",EDGE,"E72.0");var subQ14=sQuery(id+"F12.wireOp",EDGE,"E72.1");var subQ16=sQuery(id+"F12.wireOp",EDGE,"E74.1");var subQ18=sQuery(id+"F12.wireOp",EDGE,"E74.8");Q0=qUnion([makeQuery(id+"F12.imprint","IMPRINT",FACE,{"disambiguationData":[TD([[makeQuery(id+"F12.imprint","IMPRINT",EDGE,{"derivedFrom":subQ7}),1.0]])]}),makeQuery(id+"F12.imprint","IMPRINT",FACE,{"disambiguationData":[TD([[makeQuery(id+"F12.imprint","IMPRINT",EDGE,{"derivedFrom":subQ14}),1.0]])]}),makeQuery(id+"F12.imprint","IMPRINT",FACE,{"disambiguationData":[TD([[makeQuery(id+"F12.imprint","IMPRINT",EDGE,{"derivedFrom":subQ16}),1.0]])]}),makeQuery(id+"F12.imprint","IMPRINT",FACE,{"disambiguationData":[TD([[makeQuery(id+"F12.imprint","IMPRINT",EDGE,{"derivedFrom":subQ18}),-1.0]])]})]);}
            var Q1;
            Q1=makeQuery(id+"F5.boolean.opBoolean","SPLIT",FACE,{"disambiguationData":[TD([makeQuery(id+"F5.opExtrude","SWEPT_FACE",FACE,{"disambiguationData":[OSD([sQuery(id+"F4.wireOp",EDGE,"E41")])]})])],"derivedFrom":makeQuery(id+"F3.boolean.opBoolean","COPY",FACE,{"derivedFrom":makeQuery(id+"F3.opExtrude","CAP_FACE",FACE,{"disambiguationData":[OSD([sQuery(id+"F0.wireOp",EDGE,"E25.0"),sQuery(id+"F0.wireOp",EDGE,"E25.1"),sQuery(id+"F0.wireOp",EDGE,"E25.2"),sQuery(id+"F0.wireOp",EDGE,"E25.3"),sQuery(id+"F0.wireOp",EDGE,"E25.4"),sQuery(id+"F0.wireOp",EDGE,"E25.5"),sQuery(id+"F0.wireOp",EDGE,"E25.6"),sQuery(id+"F0.wireOp",EDGE,"E25.7")])],"isStart":false})})});
            extrude(context, id + "F13", {"entities" : qUnion([Q0]), "operationType" : NewBodyOperationType.REMOVE, "endBound" : BoundingType.UP_TO_SURFACE, "endBoundEntityFace" : qUnion([Q1]), "depth" : 25 * mm});
        }
        {
            var Q0;
            Q0=makeQuery(id+"F3.boolean.opBoolean","COPY",EDGE,{"derivedFrom":makeQuery(id+"F3.opExtrude","CAP_EDGE",EDGE,{"disambiguationData":[OSD([sQuery(id+"F0.wireOp",EDGE,"E25.6")])],"isStart":false})});
            var Q1;
            Q1=makeQuery(id+"F8.boolean.opBoolean","INTERSECT",EDGE,{"derivedFrom":[makeQuery(id+"F5.opExtrude","SWEPT_FACE",FACE,{"disambiguationData":[OSD([sQuery(id+"F4.wireOp",EDGE,"E30")])]}),makeQuery(id+"F8.opExtrude","CAP_FACE",FACE,{"disambiguationData":[OSD([sQuery(id+"F7.wireOp",EDGE,"E67")])],"isStart":false})]});
            var Q2;
            Q2=makeQuery(id+"F8.boolean.opBoolean","INTERSECT",EDGE,{"disambiguationData":[OD(1.0)],"derivedFrom":[makeQuery(id+"F5.opExtrude","SWEPT_FACE",FACE,{"disambiguationData":[OSD([sQuery(id+"F4.wireOp",EDGE,"E30")])]}),makeQuery(id+"F8.opExtrude","SWEPT_FACE",FACE,{"disambiguationData":[OSD([sQuery(id+"F7.wireOp",EDGE,"E67")])]})]});
            var Q3;
            {var subQ0=sQuery(id+"F4.wireOp",EDGE,"E30");Q3=makeQuery(id+"F8.boolean.opBoolean","SPLIT",EDGE,{"disambiguationData":[TD([makeQuery(id+"F5.opExtrude","SWEPT_FACE",FACE,{"disambiguationData":[OSD([sQuery(id+"F4.wireOp",EDGE,"E35.filletArc")])]})])],"derivedFrom":makeQuery(id+"F5.opExtrude","CAP_EDGE",EDGE,{"disambiguationData":[OSD([subQ0])],"isStart":false})});}
            var Q4;
            {var subQ0=sQuery(id+"F0.wireOp",EDGE,"E25.7");var subQ1=sQuery(id+"F0.wireOp",EDGE,"E25.1");var subQ2=sQuery(id+"F0.wireOp",EDGE,"E25.6");var subQ3=sQuery(id+"F0.wireOp",EDGE,"E25.5");var subQ4=sQuery(id+"F0.wireOp",EDGE,"E25.4");var subQ5=sQuery(id+"F0.wireOp",EDGE,"E25.0");var subQ6=sQuery(id+"F0.wireOp",EDGE,"E25.2");var subQ7=sQuery(id+"F0.wireOp",EDGE,"E25.3");Q4=makeQuery(id+"F8.boolean.opBoolean","INTERSECT",EDGE,{"derivedFrom":[makeQuery(id+"F5.boolean.opBoolean","SPLIT",FACE,{"disambiguationData":[TD([makeQuery(id+"F2.opExtrude","SWEPT_FACE",FACE,{"disambiguationData":[OSD([subQ5])]})])],"derivedFrom":makeQuery(id+"F3.boolean.opBoolean","COPY",FACE,{"derivedFrom":makeQuery(id+"F3.opExtrude","CAP_FACE",FACE,{"disambiguationData":[OSD([subQ5,subQ1,subQ6,subQ7,subQ4,subQ3,subQ2,subQ0])],"isStart":false})})}),makeQuery(id+"F8.opExtrude","SWEPT_FACE",FACE,{"disambiguationData":[OSD([sQuery(id+"F7.wireOp",EDGE,"E67")])]})]});}
            var Q5;
            Q5=makeQuery(id+"F8.boolean.opBoolean","INTERSECT",EDGE,{"disambiguationData":[OD(0.0)],"derivedFrom":[makeQuery(id+"F5.opExtrude","SWEPT_FACE",FACE,{"disambiguationData":[OSD([sQuery(id+"F4.wireOp",EDGE,"E30")])]}),makeQuery(id+"F8.opExtrude","SWEPT_FACE",FACE,{"disambiguationData":[OSD([sQuery(id+"F7.wireOp",EDGE,"E67")])]})]});
            fillet(context, id + "F14", {"entities" : qUnion([Q0, Q1, Q2, Q3, Q4, Q5]), "radius" : 3 * mm, "tangentPropagation" : true, "allowEdgeOverflow" : false});
        }
        {
            var Q0;
            Q0=makeQuery(id+"F1.opExtrude","CAP_EDGE",EDGE,{"disambiguationData":[OSD([sQuery(id+"F0.wireOp",EDGE,"E1.bottom")])],"isStart":false});
            fillet(context, id + "F15", {"entities" : qUnion([Q0]), "radius" : 2 * mm, "tangentPropagation" : true, "allowEdgeOverflow" : false});
        }
        {
            var Q0;
            {var subQ0=sQuery(id+"F0.wireOp",EDGE,"E22.filletArc");var subQ1=sQuery(id+"F0.wireOp",EDGE,"E7");var subQ2=sQuery(id+"F0.wireOp",EDGE,"E6");var subQ3=sQuery(id+"F0.wireOp",EDGE,"E5");var subQ4=sQuery(id+"F0.wireOp",EDGE,"E4");var subQ5=sQuery(id+"F0.wireOp",EDGE,"E1.bottom");var subQ6=sQuery(id+"F0.wireOp",EDGE,"E21.filletArc");var subQ7=sQuery(id+"F0.wireOp",EDGE,"E1.top");var subQ8=sQuery(id+"F0.wireOp",EDGE,"E1.left");var subQ9=sQuery(id+"F0.wireOp",EDGE,"E1.right");var subQ10=sQuery(id+"F0.wireOp",EDGE,"E23.filletArc");var subQ11=sQuery(id+"F0.wireOp",EDGE,"E24.filletArc");Q0=makeQuery(id+"F2.boolean.opBoolean","SPLIT",FACE,{"disambiguationData":[TD([makeQuery(id+"F1.opExtrude","SWEPT_FACE",FACE,{"disambiguationData":[OSD([subQ5])]})])],"derivedFrom":makeQuery(id+"F1.opExtrude","CAP_FACE",FACE,{"disambiguationData":[OSD([subQ5,subQ7,subQ8,subQ9,subQ4,subQ3,subQ2,subQ1,subQ6,subQ0,subQ10,subQ11])],"isStart":true})});}
            var sketch = newSketch(context, id + "F16", { "sketchPlane" : qUnion([Q0])});
            skLineSegment(sketch, "E79", {"start": v(-26.58, 74.25) * mm, "end": v(-14.92, 92.25) * mm});
            skLineSegment(sketch, "E80", {"start": v(-14.92, 92.25) * mm, "end": v(-14.92, 105.78) * mm});
            skArc(sketch, "E81", {"start": v(14.92, 105.78) * mm, "mid": v(0, 119.25) * mm, "end": v(-14.92, 105.78) * mm});
            skLineSegment(sketch, "E82", {"start": v(14.92, 105.78) * mm, "end": v(14.92, 92.25) * mm});
            skLineSegment(sketch, "E83", {"start": v(14.92, 92.25) * mm, "end": v(26.58, 74.25) * mm});
            skCircle(sketch, "E84", {"center": v(0, 104.25) * mm, "radius": 6 * mm});
            skLineSegment(sketch, "E85", {"start": v(0, 104.25) * mm, "end": v(0, 74.25) * mm, "construction": true});
            skLineSegment(sketch, "E86.MirrorCS", {"start": v(-26.58, -74.25) * mm, "end": v(-14.92, -92.25) * mm});
            skLineSegment(sketch, "E87.MirrorCS", {"start": v(-14.92, -92.25) * mm, "end": v(-14.92, -105.78) * mm});
            skArc(sketch, "E88.MirrorCS", {"start": v(14.92, -105.78) * mm, "mid": v(0, -119.25) * mm, "end": v(-14.92, -105.78) * mm});
            skLineSegment(sketch, "E89.MirrorCS", {"start": v(14.92, -105.78) * mm, "end": v(14.92, -92.25) * mm});
            skLineSegment(sketch, "E90.MirrorCS", {"start": v(0, -104.25) * mm, "end": v(0, -74.25) * mm, "construction": true});
            skLineSegment(sketch, "E91.MirrorCS", {"start": v(14.92, -92.25) * mm, "end": v(26.58, -74.25) * mm});
            skCircle(sketch, "E92.MirrorC", {"center": v(0, -104.25) * mm, "radius": 6 * mm});
            skSolve(sketch);
        }
        {
            var Q0;
            {var subQ0=sQuery(id+"F16.wireOp",EDGE,"E86.MirrorCS");Q0=makeQuery(id+"F16.imprint","IMPRINT",FACE,{"disambiguationData":[TD([[makeQuery(id+"F16.imprint","IMPRINT",EDGE,{"derivedFrom":subQ0}),1.0]])]});}
            var Q1;
            {var subQ0=sQuery(id+"F16.wireOp",EDGE,"E79");Q1=makeQuery(id+"F16.imprint","IMPRINT",FACE,{"disambiguationData":[TD([[makeQuery(id+"F16.imprint","IMPRINT",EDGE,{"derivedFrom":subQ0}),-1.0]])]});}
            var Q2;
            Q2=makeQuery(id+"F16.imprint","IMPRINT",FACE,{"disambiguationData":[TD([[makeQuery(id+"F16.imprint","IMPRINT",EDGE,{"derivedFrom":makeQuery(id+"F1.opExtrude","CAP_EDGE",EDGE,{"disambiguationData":[OSD([sQuery(id+"F0.wireOp",EDGE,"E1.left")])],"isStart":true})}),-1.0]])]});
            var Q3;
            {var subQ0=sQuery(id+"F0.wireOp",EDGE,"E22.filletArc");var subQ1=sQuery(id+"F0.wireOp",EDGE,"E7");var subQ2=sQuery(id+"F0.wireOp",EDGE,"E6");var subQ3=sQuery(id+"F0.wireOp",EDGE,"E5");var subQ4=sQuery(id+"F0.wireOp",EDGE,"E4");var subQ5=sQuery(id+"F0.wireOp",EDGE,"E1.bottom");var subQ6=sQuery(id+"F0.wireOp",EDGE,"E21.filletArc");var subQ7=sQuery(id+"F0.wireOp",EDGE,"E1.top");var subQ8=sQuery(id+"F0.wireOp",EDGE,"E1.left");var subQ9=sQuery(id+"F0.wireOp",EDGE,"E1.right");var subQ10=sQuery(id+"F0.wireOp",EDGE,"E23.filletArc");var subQ11=sQuery(id+"F0.wireOp",EDGE,"E24.filletArc");Q3=makeQuery(id+"F2.boolean.opBoolean","SPLIT",FACE,{"disambiguationData":[TD([makeQuery(id+"F1.opExtrude","SWEPT_FACE",FACE,{"disambiguationData":[OSD([subQ5])]})])],"derivedFrom":makeQuery(id+"F1.opExtrude","CAP_FACE",FACE,{"disambiguationData":[OSD([subQ5,subQ7,subQ8,subQ9,subQ4,subQ3,subQ2,subQ1,subQ6,subQ0,subQ10,subQ11])],"isStart":true})});}
            extrude(context, id + "F17", {"entities" : qUnion([Q0, Q1, Q2]), "endBoundEntityFace" : qUnion([Q3]), "depth" : 1.48 * mm});
        }
    });
